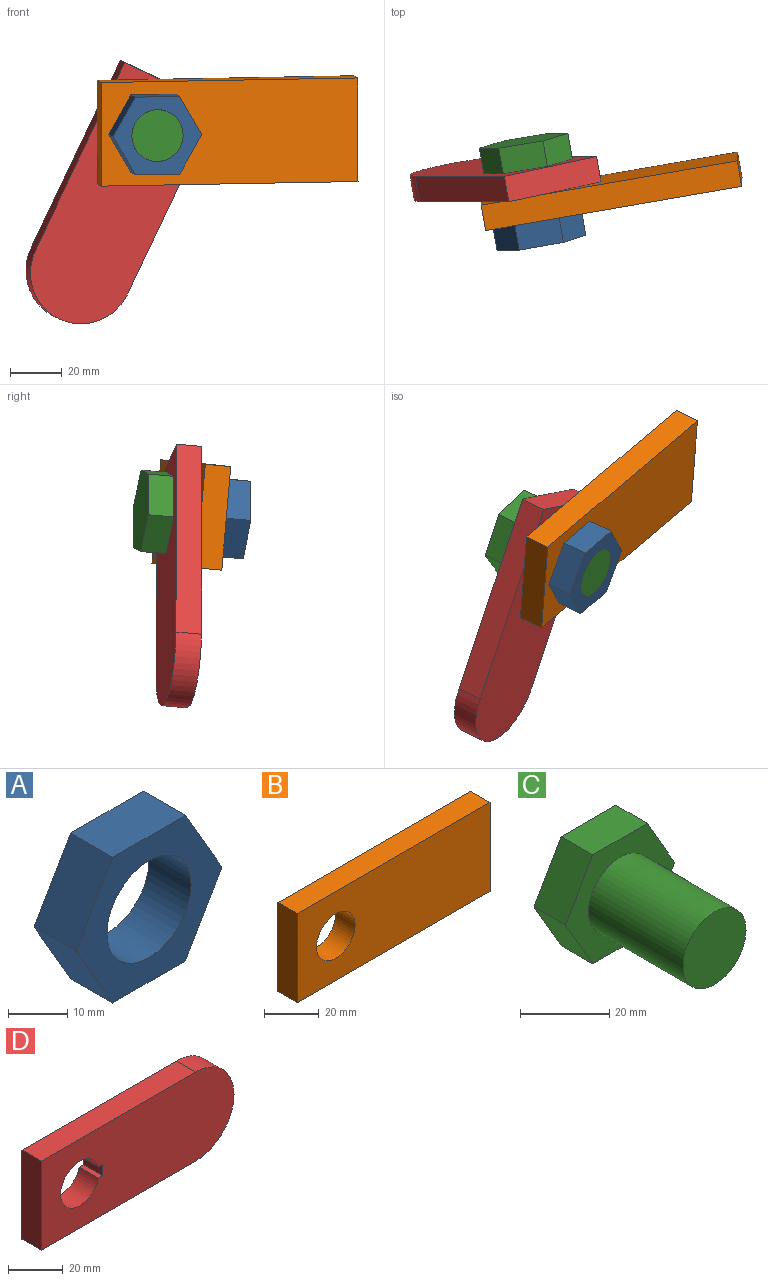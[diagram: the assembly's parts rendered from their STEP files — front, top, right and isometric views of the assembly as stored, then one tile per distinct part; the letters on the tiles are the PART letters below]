
ASSEMBLY  parts=4 mates=3
PART A: 9 faces, bbox 34.6x10x30 mm
  f0: plane 15x10mm, normal (-0.87,0,0.5), area 173.2mm2, adj f1,f6,f7,f8
  f1: plane 15x10mm, normal (-0.87,0,-0.5), area 173.2mm2, adj f0,f2,f7,f8
  f2: plane 17.32x10mm, normal (0,0,-1), area 173.2mm2, adj f1,f3,f7,f8
  f3: plane 15x10mm, normal (0.87,0,-0.5), area 173.2mm2, adj f2,f4,f7,f8
  f4: plane 15x10mm, normal (0.87,0,0.5), area 173.2mm2, adj f3,f6,f7,f8
  f5: cylinder r=10mm len=20mm, axis (0,1,0), area 628.3mm2, adj f7,f8
  f6: plane 17.32x10mm, normal (0,0,1), area 173.2mm2, adj f0,f4,f7,f8
  f7: plane 34.64x30mm, normal (0,-1,0), area 465.3mm2, adj f0,f1,f2,f3,f4,f5,f6
  f8: plane 34.64x30mm, normal (0,1,0), area 465.3mm2, adj f0,f1,f2,f3,f4,f5,f6
PART B: 7 faces, bbox 100x10x40 mm
  f0: plane 100x10mm, normal (0,0,1), area 1000mm2, adj f1,f4,f5,f6
  f1: plane 40x10mm, normal (-1,0,0), area 400mm2, adj f0,f2,f5,f6
  f2: plane 100x10mm, normal (0,0,-1), area 1000mm2, adj f1,f4,f5,f6
  f3: cylinder r=10mm len=20mm, axis (0,1,0), area 628.3mm2, adj f5,f6
  f4: plane 40x10mm, normal (1,0,0), area 400mm2, adj f0,f2,f5,f6
  f5: plane 100x40mm, normal (0,-1,0), area 3685.8mm2, adj f0,f1,f2,f3,f4
  f6: plane 100x40mm, normal (0,1,0), area 3685.8mm2, adj f0,f1,f2,f3,f4
PART C: 14 faces, bbox 34.6x40x30 mm
  f0: cylinder r=10mm len=30mm, axis (0,1,0), area 1834.4mm2, adj f7,f9,f10,f11,f12
  f1: plane 15x10mm, normal (-0.87,0,0.5), area 173.2mm2, adj f2,f6,f7,f8
  f2: plane 15x10mm, normal (-0.87,0,-0.5), area 173.2mm2, adj f1,f3,f7,f8
  f3: plane 17.32x10mm, normal (0,0,-1), area 173.2mm2, adj f2,f4,f7,f8
  f4: plane 15x10mm, normal (0.87,0,-0.5), area 173.2mm2, adj f3,f5,f7,f8
  f5: plane 15x10mm, normal (0.87,0,0.5), area 173.2mm2, adj f4,f6,f7,f8
  f6: plane 17.32x10mm, normal (0,0,1), area 173.2mm2, adj f1,f5,f7,f8
  f7: plane 34.64x30mm, normal (0,-1,0), area 455.7mm2, adj f0,f1,f2,f3,f4,f5,f6,f11
  f8: plane 34.64x30mm, normal (0,1,0), area 779.4mm2, adj f1,f2,f3,f4,f5,f6
  f9: plane 20x20mm, normal (0,-1,0), area 314.2mm2, adj f0
  f10: plane 5x2.12mm, normal (0,-1,0), area 9.5mm2, adj f0,f11,f12,f13
  f11: plane 10x2.12mm, normal (0,0,1), area 21.2mm2, adj f0,f7,f10,f13
  f12: plane 10x2.12mm, normal (0,0,-1), area 21.2mm2, adj f0,f7,f10,f13
  f13: plane 10x5mm, normal (1,0,0), area 50mm2, adj f7,f10,f11,f12
PART D: 10 faces, bbox 100x10x40 mm
  f0: plane 10x5mm, normal (-1,0,0), area 50mm2, adj f1,f7,f8,f9
  f1: plane 10x2.32mm, normal (0,0,1), area 23.2mm2, adj f0,f2,f8,f9
  f2: cylinder r=10mm len=20mm, axis (0,1,0), area 577.8mm2, adj f1,f7,f8,f9
  f3: plane 40x10mm, normal (-1,0,0), area 400mm2, adj f4,f6,f8,f9
  f4: plane 80x10mm, normal (0,0,-1), area 800mm2, adj f3,f5,f8,f9
  f5: cylinder r=20mm len=40mm, axis (0,1,0), area 628.3mm2, adj f4,f6,f8,f9
  f6: plane 80x10mm, normal (0,0,1), area 800mm2, adj f3,f5,f8,f9
  f7: plane 10x2.32mm, normal (0,0,-1), area 23.2mm2, adj f0,f2,f8,f9
  f8: plane 100x40mm, normal (0,-1,0), area 3503.6mm2, adj f0,f1,f2,f3,f4,f5,f6,f7
  f9: plane 100x40mm, normal (0,1,0), area 3503.6mm2, adj f0,f1,f2,f3,f4,f5,f6,f7
PLACE A rot(axis=(0.45,-0.05,0.89),11deg) t=(220.17,100.91,32.6)mm
PLACE B rot(axis=(0.45,-0.05,0.89),11deg) t=(198.81,109.04,13.16)mm fixed
PLACE C rot(axis=(-0.06,0.99,0.1),115.7deg) t=(215.02,130.36,35.13)mm
PLACE D rot(axis=(0.53,0.08,-0.84),174.3deg) t=(210.44,114.72,-29.16)mm
MATE revolute A.f5 <-> B.f3  axis (-0.17,0.98,0.08) through (220.17,100.91,32.6)mm
MATE revolute B.f3 <-> D.f2  axis (-0.17,0.98,0.08) through (218.45,110.73,33.44)mm
MATE fastened D.f2 <-> C.f0  axis (-0.17,0.98,0.08) through (216.74,120.54,34.29)mm
